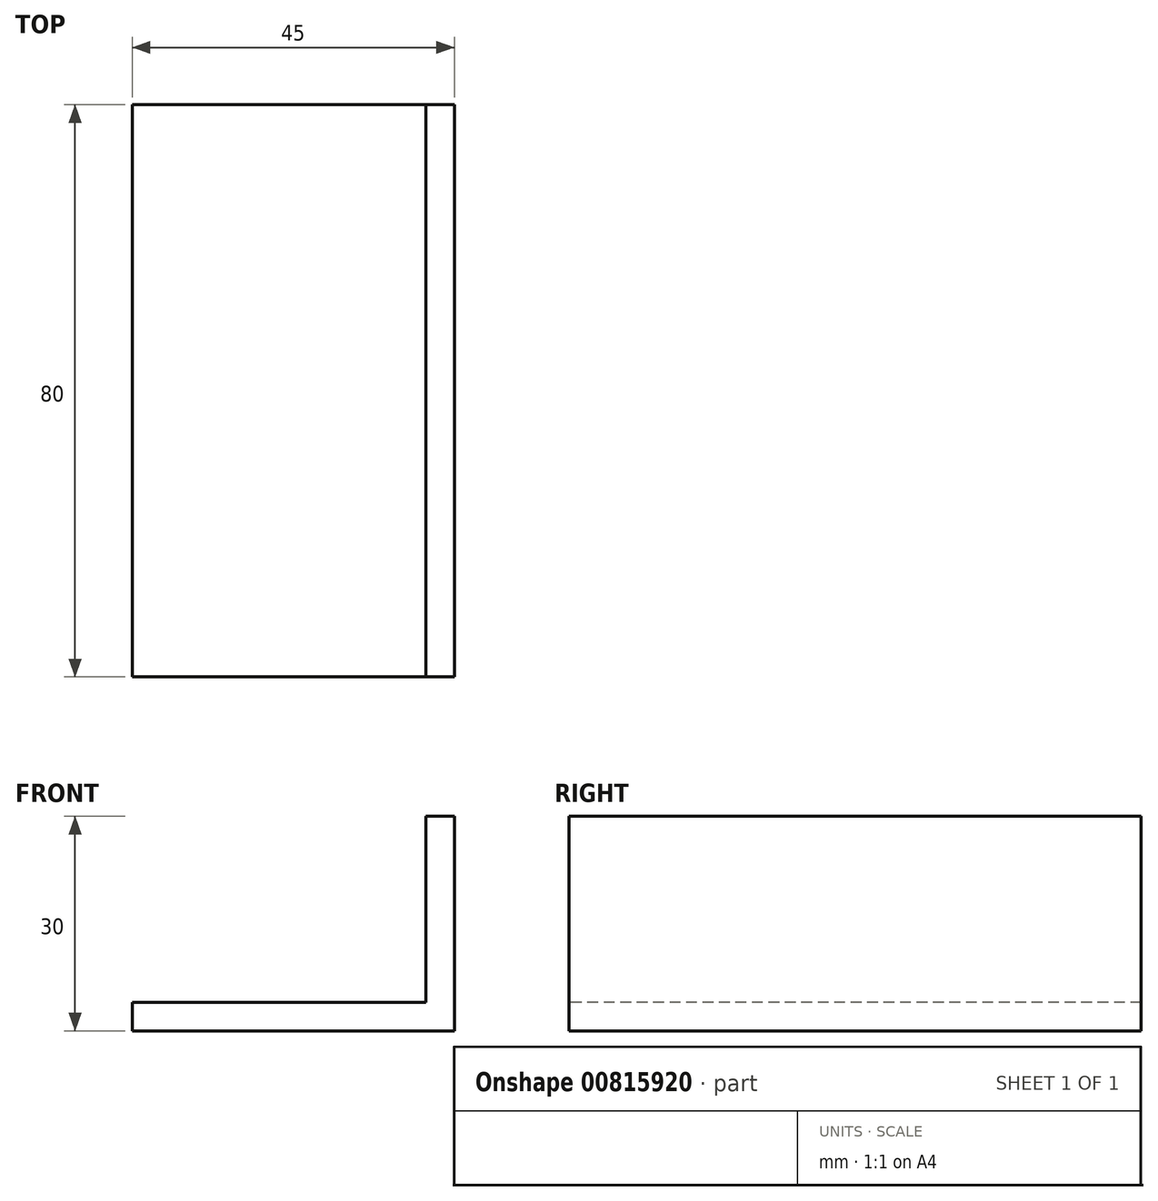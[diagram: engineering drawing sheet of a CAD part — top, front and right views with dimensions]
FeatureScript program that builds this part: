
annotation { "Feature Type Name" : "Feature", "Feature Type Description" : "" }
export const myFeature = defineFeature(function(context is Context, id is Id, definition is map)
    precondition{}
    {
        {
            var Q0;
            Q0=qCreatedBy(makeId("Front.planeOp"),FACE);
            var sketch = newSketch(context, id + "F0", { "sketchPlane" : qUnion([Q0])});
            skLineSegment(sketch, "E0", {"start": v(0, 0) * mm, "end": v(45, 0) * mm});
            skLineSegment(sketch, "E1", {"start": v(45, 0) * mm, "end": v(45, 30) * mm});
            skLineSegment(sketch, "E2.0", {"start": v(41, 4) * mm, "end": v(41, 30) * mm});
            skLineSegment(sketch, "E2.1", {"start": v(0, 4) * mm, "end": v(41, 4) * mm});
            skLineSegment(sketch, "E3", {"start": v(0, 0) * mm, "end": v(0, 4) * mm});
            skLineSegment(sketch, "E4", {"start": v(41, 30) * mm, "end": v(45, 30) * mm});
            skSolve(sketch);
        }
        {
            var Q0;
            Q0=qSketchRegion(id+"F0",true);
            extrude(context, id + "F1", {"entities" : qUnion([Q0]), "oppositeDirection" : true, "depth" : 80 * mm, "offsetDistance" : 25.4 * mm});
        }
    });
